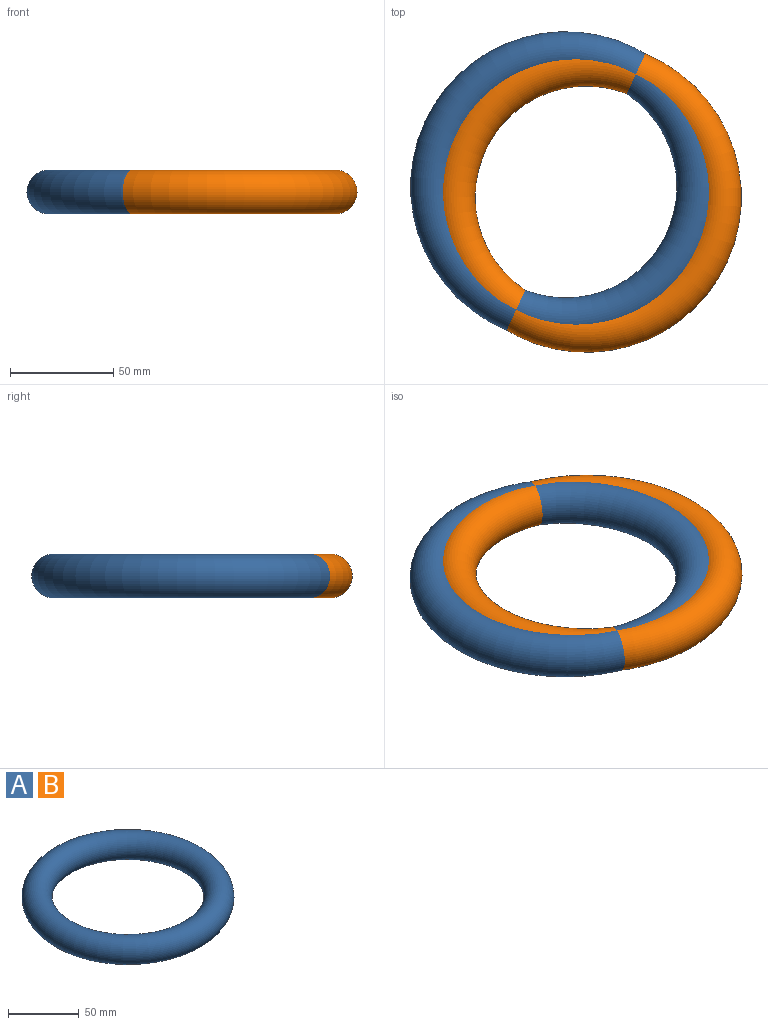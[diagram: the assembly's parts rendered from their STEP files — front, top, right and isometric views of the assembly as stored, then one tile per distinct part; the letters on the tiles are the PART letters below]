
ASSEMBLY  parts=2 mates=1
PART A: 1 faces, bbox 162.2x162.2x21.2 mm
  f0: torus R=64.32mm, axis (0,0,-1), area 26957.5mm2
PART B: same geometry as A
PLACE A rot(axis=(0,0,-1),180deg) t=(-9.93,-86.37,203.2)mm
PLACE B t=(0,-91.44,203.2)mm fixed
MATE planar A.f0 <-> B.f0  axis (0,0,-1) through (-9.93,-86.37,212.76)mm
